# Revit family: e763fb95_9a51_4f95_9eb1_2153df20e182
name_source: partatom
category: Generic Models
revit_build: Autodesk Revit Architecture 2015 (Build: 20140606_1530(x64)
units: mm (PartAtom-declared; Revit-internal decimal feet)

## types (1)
- Default
    BIMobject category = Office Furniture
    BOSUseNativeGeometries = 0
    Date of publishing = 2016-03-29
    Design country = Spain
    Edition number = 1
    IFC Classification = Furniture
    Manufacturer country = Spain
    Manufacturer name = Actiu
    Material main = Aluminium
    Material secondary = MDF
    Nominal height = 740
    Nominal width = 3200
    OmniClass Code = 23-21 13 25
    OmniClass Description = Office Equipment
    Product Guid = b36352ad-ba10-47d1-9d5b-5ec8b9d00b31
    Product SKU = longotwindesks
    Product certification = http://www.actiu.com
    Product data url = https://bimobject.com
    Product family = Desks
    Product group = Desk
    Product name = Longo Twin Desks
    QR code = http://bimobject.com
    Technical description = http://www.actiu.com
    UNSPSC Code = 56
    Uniclass 1.4 Code = L8211
    Uniclass 1.4 Description = Furniture
    Weight Net (Kg) = 0
    Youtube clip = https://www.youtube.com

## geometry (parser evidence)
native form markers: Sweep x2
no freeform markers — native parametric forms only
